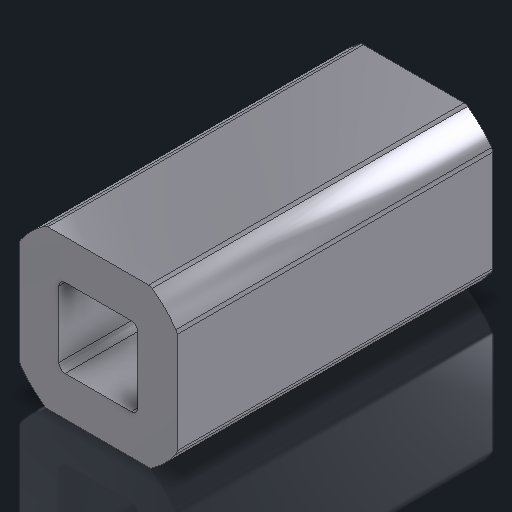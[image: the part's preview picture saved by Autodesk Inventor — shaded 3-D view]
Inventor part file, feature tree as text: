
AUTODESK INVENTOR PART (.ipt)
format: ipt  version: 2023.2 (Build 272271030, 271C)  size: 182,272 bytes
history: native  units: in
note: dims shown in document units (in); Inventor stores cm internally (conversion verified against a paired STEP export)
features: extrude x2, sketch x2, fillet x1
ambient origin geometry x8: Origin, YZ Plane, XZ Plane, XY Plane, X Axis, Y Axis, Z Axis, Center Point
bodies: Solid1 (feature_tree)
feature tree (5):
  extrude  "Extrusion1"  Depth=0.25in
  extrude  "Extrusion2"  Depth=0.5in TaperAngle=0.0deg
  fillet  "Fillet1"  Radius=0.125in
  sketch  "Sketch1"  dims[d0=0.3in d1=0.25in]
  sketch  "Sketch2"  dims[d2=0.5in d3=0.0in d5=0.5in d6=0.0in d7=0.125in d8=0.01in]
